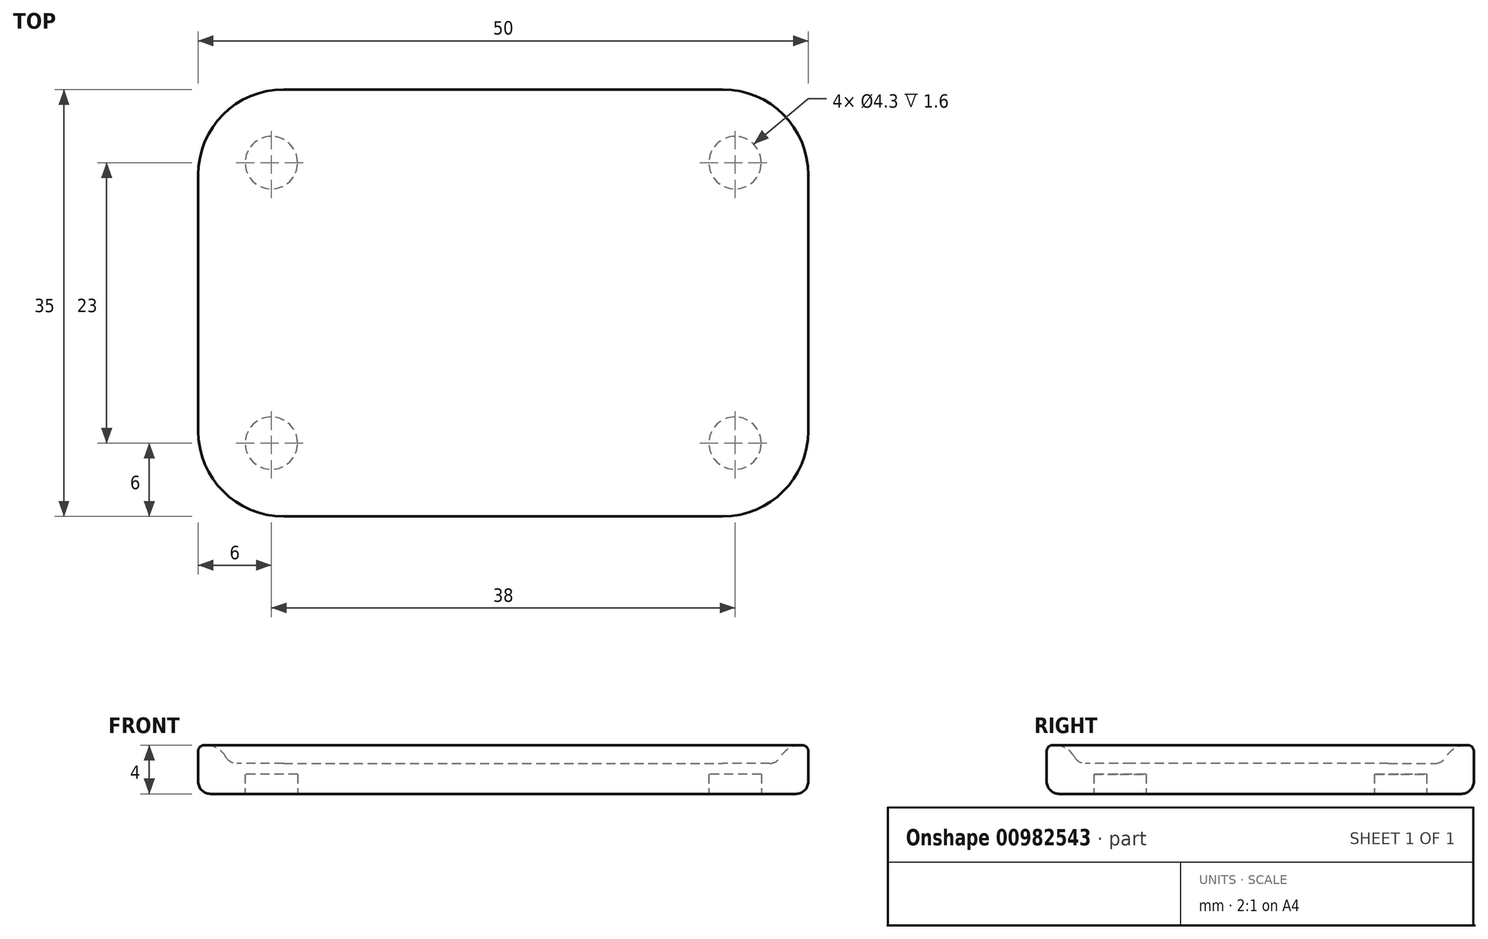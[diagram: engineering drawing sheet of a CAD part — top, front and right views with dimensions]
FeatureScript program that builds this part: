
annotation { "Feature Type Name" : "Feature", "Feature Type Description" : "" }
export const myFeature = defineFeature(function(context is Context, id is Id, definition is map)
    precondition{}
    {
        {
            var Q0;
            Q0=qCreatedBy(makeId("Top.planeOp"),FACE);
            var sketch = newSketch(context, id + "F0", { "sketchPlane" : qUnion([Q0])});
            skLineSegment(sketch, "E0.bottom", {"start": v(18, -17.5) * mm, "end": v(-18, -17.5) * mm});
            skLineSegment(sketch, "E0.top", {"start": v(18, 17.5) * mm, "end": v(-18, 17.5) * mm});
            skLineSegment(sketch, "E0.left", {"start": v(25, -10.5) * mm, "end": v(25, 10.5) * mm});
            skLineSegment(sketch, "E0.right", {"start": v(-25, -10.5) * mm, "end": v(-25, 10.5) * mm});
            skPoint(sketch, "E0.middle", {"position": v(0, 0) * mm});
            skPoint(sketch, "E1.visualSharp", {"position": v(25, 17.5) * mm});
            skArc(sketch, "E1.filletArc", {"start": v(25, 10.5) * mm, "mid": v(22.95, 15.45) * mm, "end": v(18, 17.5) * mm});
            skPoint(sketch, "E2.visualSharp", {"position": v(25, -17.5) * mm});
            skArc(sketch, "E2.filletArc", {"start": v(18, -17.5) * mm, "mid": v(22.95, -15.45) * mm, "end": v(25, -10.5) * mm});
            skPoint(sketch, "E3.visualSharp", {"position": v(-25, -17.5) * mm});
            skArc(sketch, "E3.filletArc", {"start": v(-25, -10.5) * mm, "mid": v(-22.95, -15.45) * mm, "end": v(-18, -17.5) * mm});
            skPoint(sketch, "E4.visualSharp", {"position": v(-25, 17.5) * mm});
            skArc(sketch, "E4.filletArc", {"start": v(-18, 17.5) * mm, "mid": v(-22.95, 15.45) * mm, "end": v(-25, 10.5) * mm});
            skSolve(sketch);
        }
        {
            var Q0;
            Q0 = qSketchRegion(id + "F0", true);
            extrude(context, id + "F1", {"entities" : qUnion([Q0]), "depth" : 4 * mm, "offsetDistance" : 25 * mm});
        }
        {
            var Q0;
            Q0=makeQuery(id+"F1.opExtrude","CAP_EDGE",EDGE,{"disambiguationData":[OSD([sQuery(id+"F0.wireOp",EDGE,"E0.bottom")])],"isStart":true});
            fillet(context, id + "F2", {"entities" : qUnion([Q0]), "radius" : 1 * mm, "tangentPropagation" : true, "allowEdgeOverflow" : false});
        }
        {
            var Q0;
            Q0=makeQuery(id+"F1.opExtrude","CAP_FACE",FACE,{"disambiguationData":[OSD([sQuery(id+"F0.wireOp",EDGE,"E0.bottom"),sQuery(id+"F0.wireOp",EDGE,"E0.top"),sQuery(id+"F0.wireOp",EDGE,"E0.left"),sQuery(id+"F0.wireOp",EDGE,"E0.right"),sQuery(id+"F0.wireOp",EDGE,"E1.filletArc"),sQuery(id+"F0.wireOp",EDGE,"E2.filletArc"),sQuery(id+"F0.wireOp",EDGE,"E3.filletArc"),sQuery(id+"F0.wireOp",EDGE,"E4.filletArc")])],"isStart":false});
            shell(context, id + "F3", {"entities" : qUnion([Q0]), "thickness" : 2.5 * mm});
        }
        {
            var Q0;
            Q0=makeQuery(id+"F3.opShell","OFFSET_EDGE",EDGE,{"disambiguationData":[OSD([sQuery(id+"F0.wireOp",EDGE,"E0.top")])]});
            fillet(context, id + "F4", {"entities" : qUnion([Q0]), "radius" : 2 * mm, "tangentPropagation" : true, "allowEdgeOverflow" : false});
        }
        {
            var Q0;
            {var subQ0=sQuery(id+"F0.wireOp",EDGE,"E0.top");Q0=makeQuery(id+"F4.opFillet","BLEND_EDGE",EDGE,{"blendedFrom":[makeQuery(id+"F3.opShell","OFFSET_EDGE",EDGE,{"disambiguationData":[OSD([subQ0])]}),makeQuery(id+"F3.opShell","OFFSET_FACE",FACE,{"disambiguationData":[OSD([sQuery(id+"F0.wireOp",EDGE,"E0.bottom"),subQ0,sQuery(id+"F0.wireOp",EDGE,"E0.left"),sQuery(id+"F0.wireOp",EDGE,"E0.right"),sQuery(id+"F0.wireOp",EDGE,"E1.filletArc"),sQuery(id+"F0.wireOp",EDGE,"E2.filletArc"),sQuery(id+"F0.wireOp",EDGE,"E3.filletArc"),sQuery(id+"F0.wireOp",EDGE,"E4.filletArc")])]})],"blendedInto":[makeQuery(id+"F3.opShell","OFFSET_FACE",FACE,{"disambiguationData":[OSD([sQuery(id+"F0.wireOp",EDGE,"E0.bottom"),subQ0,sQuery(id+"F0.wireOp",EDGE,"E0.left"),sQuery(id+"F0.wireOp",EDGE,"E0.right"),sQuery(id+"F0.wireOp",EDGE,"E1.filletArc"),sQuery(id+"F0.wireOp",EDGE,"E2.filletArc"),sQuery(id+"F0.wireOp",EDGE,"E3.filletArc"),sQuery(id+"F0.wireOp",EDGE,"E4.filletArc")])]})]});}
            fillet(context, id + "F5", {"entities" : qUnion([Q0]), "radius" : 1 * mm, "tangentPropagation" : true, "allowEdgeOverflow" : false});
        }
        {
            var Q0;
            Q0=makeQuery(id+"F1.opExtrude","CAP_EDGE",EDGE,{"disambiguationData":[OSD([sQuery(id+"F0.wireOp",EDGE,"E0.bottom")])],"isStart":false});
            fillet(context, id + "F6", {"entities" : qUnion([Q0]), "radius" : 0.5 * mm, "tangentPropagation" : true, "allowEdgeOverflow" : false});
        }
        {
            var Q0;
            Q0=makeQuery(id+"F0.imprint","IMPRINT",FACE,{"disambiguationData":[TD([[makeQuery(id+"F0.imprint","IMPRINT",EDGE,{"derivedFrom":sQuery(id+"F0.wireOp",EDGE,"E0.bottom")}),-1.0]])]});
            var sketch = newSketch(context, id + "F7", { "sketchPlane" : qUnion([Q0])});
            skLineSegment(sketch, "E5.bottom", {"start": v(19, 11.5) * mm, "end": v(-19, 11.5) * mm, "construction": true});
            skLineSegment(sketch, "E5.top", {"start": v(19, -11.5) * mm, "end": v(-19, -11.5) * mm, "construction": true});
            skLineSegment(sketch, "E5.left", {"start": v(19, 11.5) * mm, "end": v(19, -11.5) * mm, "construction": true});
            skLineSegment(sketch, "E5.right", {"start": v(-19, 11.5) * mm, "end": v(-19, -11.5) * mm, "construction": true});
            skPoint(sketch, "E5.middle", {"position": v(0, 0) * mm});
            skCircle(sketch, "E6", {"center": v(-19, -11.5) * mm, "radius": 2.15 * mm});
            skCircle(sketch, "E7", {"center": v(19, -11.5) * mm, "radius": 2.15 * mm});
            skCircle(sketch, "E8", {"center": v(-19, 11.5) * mm, "radius": 2.15 * mm});
            skCircle(sketch, "E9", {"center": v(19, 11.5) * mm, "radius": 2.15 * mm});
            skSolve(sketch);
        }
        {
            var Q0;
            Q0 = qSketchRegion(id + "F7", true);
            extrude(context, id + "F8", {"entities" : qUnion([Q0]), "operationType" : NewBodyOperationType.REMOVE, "depth" : 1.6 * mm, "offsetDistance" : 25 * mm});
        }
    });
